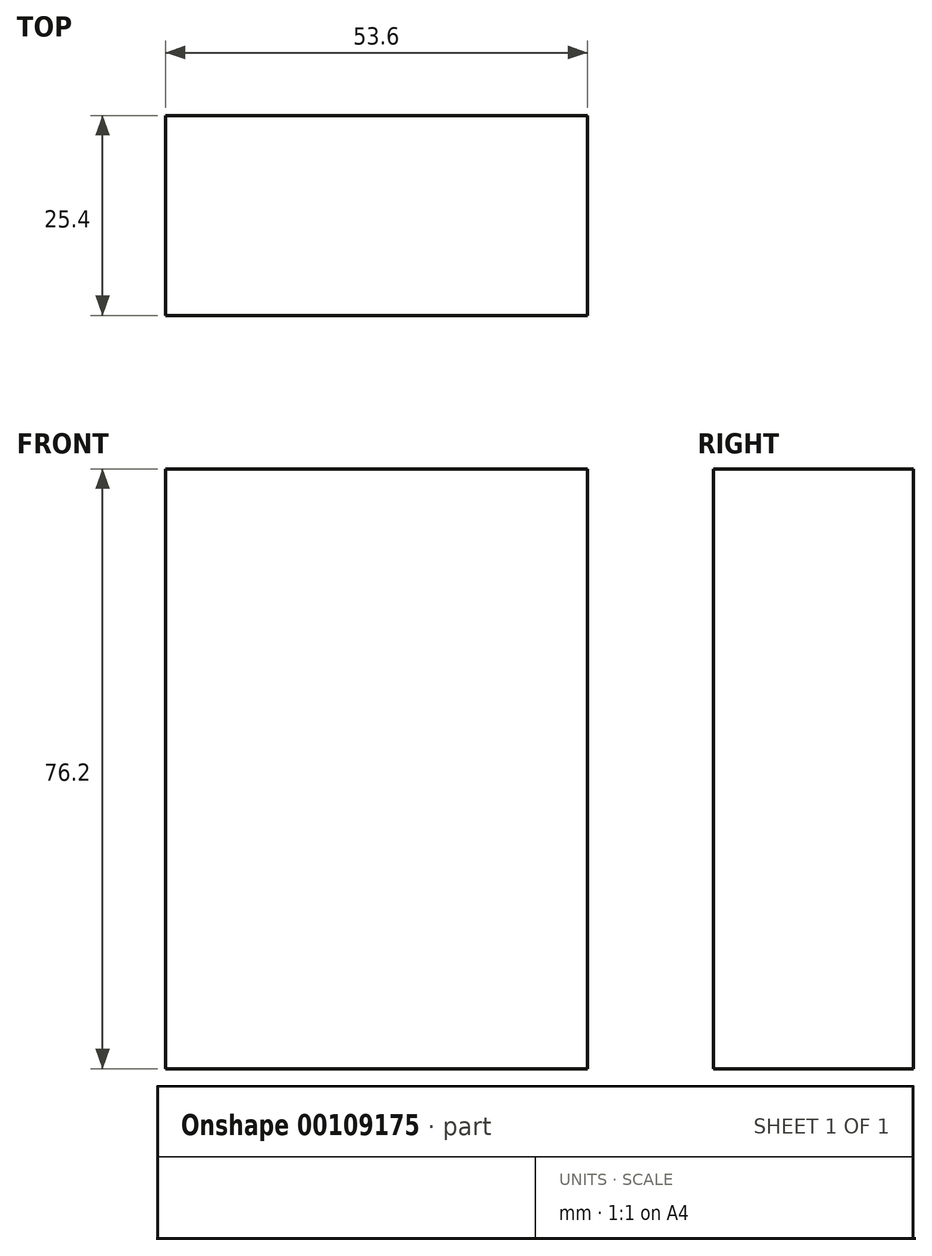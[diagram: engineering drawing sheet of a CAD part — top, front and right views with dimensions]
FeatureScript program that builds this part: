
annotation { "Feature Type Name" : "Feature", "Feature Type Description" : "" }
export const myFeature = defineFeature(function(context is Context, id is Id, definition is map)
    precondition{}
    {
        {
            var Q0;
            Q0=qCreatedBy(makeId("Top.planeOp"),FACE);
            var sketch = newSketch(context, id + "F0", { "sketchPlane" : qUnion([Q0])});
            skLineSegment(sketch, "E0.bottom", {"start": v(-27.31, 15.4) * mm, "end": v(26.29, 15.4) * mm});
            skLineSegment(sketch, "E0.top", {"start": v(-27.31, -10) * mm, "end": v(26.29, -10) * mm});
            skLineSegment(sketch, "E0.left", {"start": v(-27.31, 15.4) * mm, "end": v(-27.31, -10) * mm});
            skLineSegment(sketch, "E0.right", {"start": v(26.29, 15.4) * mm, "end": v(26.29, -10) * mm});
            skSolve(sketch);
        }
        {
            var Q0;
            Q0 = qSketchRegion(id + "F0", true);
            extrude(context, id + "F1", {"entities" : qUnion([Q0]), "depth" : 76.2 * mm});
        }
    });
